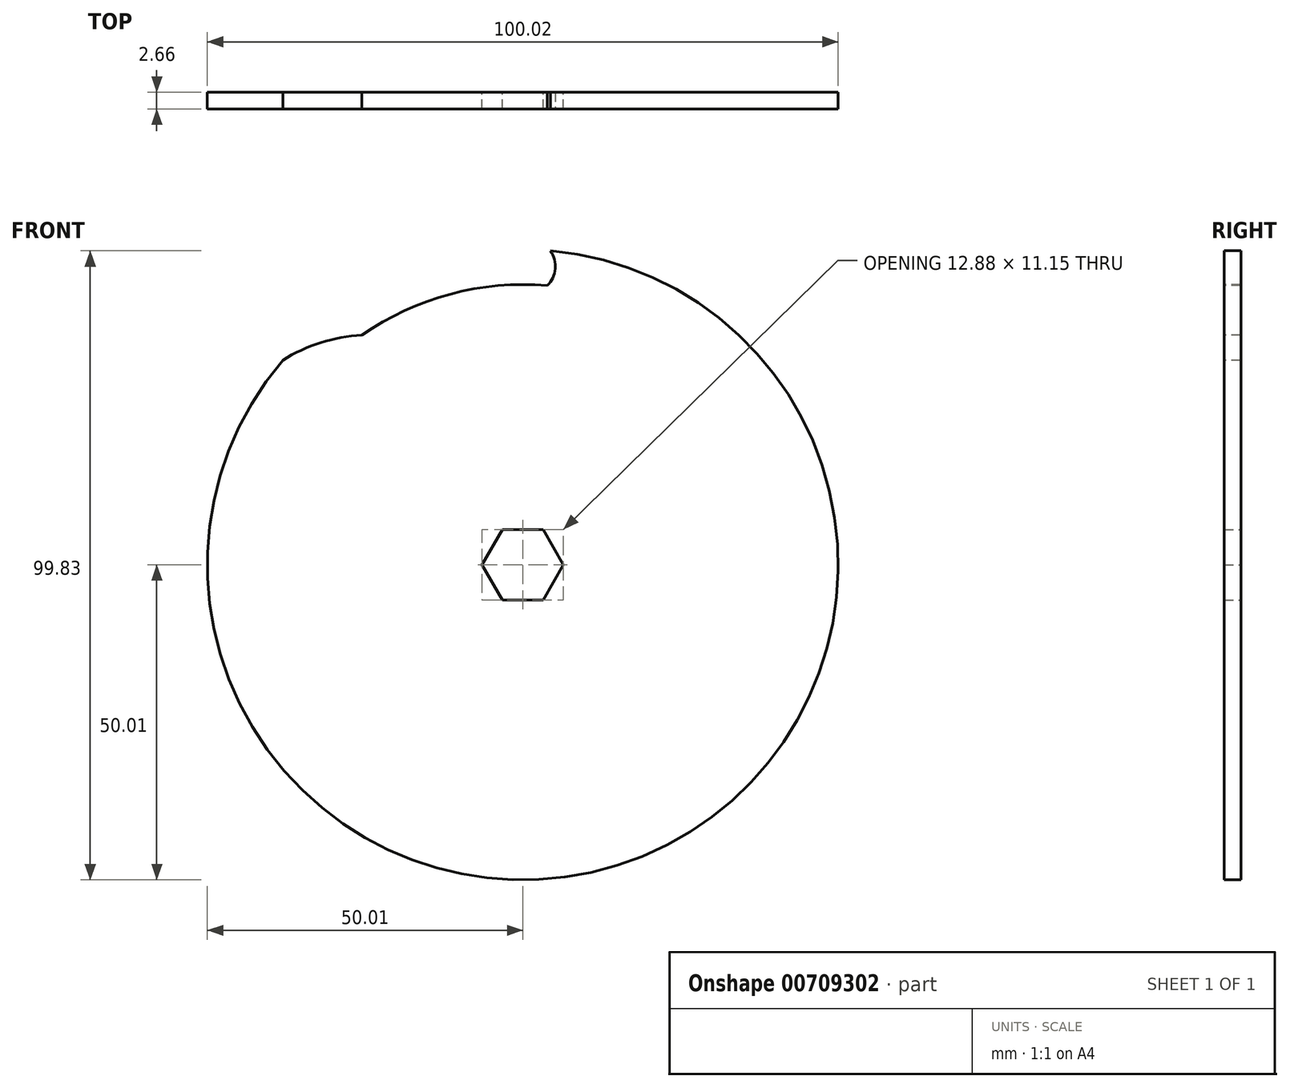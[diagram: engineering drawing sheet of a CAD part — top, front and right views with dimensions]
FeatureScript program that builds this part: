
annotation { "Feature Type Name" : "Feature", "Feature Type Description" : "" }
export const myFeature = defineFeature(function(context is Context, id is Id, definition is map)
    precondition{}
    {
        {
            var Q0;
            Q0=qCreatedBy(makeId("Front.planeOp"),FACE);
            var sketch = newSketch(context, id + "F0", { "sketchPlane" : qUnion([Q0])});
            skCircle(sketch, "E0", {"center": v(0, 0) * mm, "radius": 50 * mm});
            skCircle(sketch, "E1", {"center": v(0, 0) * mm, "radius": 44.45 * mm, "construction": true});
            skCircle(sketch, "E2", {"center": v(0, 0) * mm, "radius": 47.23 * mm, "construction": true});
            skLineSegment(sketch, "E3", {"start": v(0, 0) * mm, "end": v(3.87, 44.28) * mm, "construction": true});
            skLineSegment(sketch, "E4", {"start": v(3.87, 44.28) * mm, "end": v(4.12, 47.05) * mm, "construction": true});
            skLineSegment(sketch, "E5", {"start": v(4.12, 47.05) * mm, "end": v(4.36, 49.82) * mm, "construction": true});
            skArc(sketch, "E6", {"start": v(3.87, 44.28) * mm, "mid": v(5.15, 46.96) * mm, "end": v(4.36, 49.82) * mm, "construction": true});
            skCircle(sketch, "E7", {"center": v(0, 0) * mm, "radius": 6.38 * mm, "construction": true});
            skLineSegment(sketch, "E8", {"start": v(0, 0) * mm, "end": v(-36.41, 25.5) * mm, "construction": true});
            skLineSegment(sketch, "E9", {"start": v(0, 0) * mm, "end": v(-25.5, 36.41) * mm, "construction": true});
            skLineSegment(sketch, "E10", {"start": v(-36.41, 25.5) * mm, "end": v(-40.96, 28.68) * mm, "construction": true});
            skArc(sketch, "E11", {"start": v(-25.5, 36.41) * mm, "mid": v(-32.03, 35.26) * mm, "end": v(-38.05, 32.45) * mm, "construction": true});
            skCircle(sketch, "E12.cCircle", {"center": v(0, 0) * mm, "radius": 5.58 * mm, "construction": true});
            skLineSegment(sketch, "E12.0", {"start": v(-3.22, 5.58) * mm, "end": v(3.22, 5.58) * mm});
            skLineSegment(sketch, "E12.1", {"start": v(3.22, 5.58) * mm, "end": v(6.44, 0) * mm});
            skLineSegment(sketch, "E12.2", {"start": v(6.44, 0) * mm, "end": v(3.22, -5.58) * mm});
            skLineSegment(sketch, "E12.3", {"start": v(3.22, -5.58) * mm, "end": v(-3.22, -5.58) * mm});
            skLineSegment(sketch, "E12.4", {"start": v(-3.22, -5.58) * mm, "end": v(-6.44, 0) * mm});
            skLineSegment(sketch, "E12.5", {"start": v(-6.44, 0) * mm, "end": v(-3.22, 5.58) * mm});
            skPoint(sketch, "E12.0.midPoint", {"position": v(0, 5.58) * mm});
            skLineSegment(sketch, "E13", {"start": v(0, 0) * mm, "end": v(0, 44.45) * mm, "construction": true});
            skSolve(sketch);
        }
        {
            var Q0;
            Q0=qSketchRegion(id+"F0",true);
            extrude(context, id + "F1", {"entities" : qUnion([Q0]), "depth" : 2.67 * mm, "offsetDistance" : 25.4 * mm, "symmetric" : true});
        }
        {
            var Q0;
            Q0=qCreatedBy(makeId("Front.planeOp"),FACE);
            var sketch = newSketch(context, id + "F2", { "sketchPlane" : qUnion([Q0])});
            skArc(sketch, "E14", {"start": v(3.87, 44.28) * mm, "mid": v(-11.5, 42.94) * mm, "end": v(-25.5, 36.41) * mm});
            skArc(sketch, "E15", {"start": v(3.87, 44.28) * mm, "mid": v(5.15, 46.96) * mm, "end": v(4.36, 49.82) * mm});
            skArc(sketch, "E16", {"start": v(-25.5, 36.41) * mm, "mid": v(-32.03, 35.26) * mm, "end": v(-38.05, 32.45) * mm});
            skArc(sketch, "E17", {"start": v(4.36, 49.82) * mm, "mid": v(-18.95, 46.28) * mm, "end": v(-38.05, 32.45) * mm});
            skLineSegment(sketch, "E18", {"start": v(0, 0) * mm, "end": v(-3.87, 44.28) * mm, "construction": true});
            skSolve(sketch);
        }
        {
            var Q0;
            Q0=qSketchRegion(id+"F2",true);
            extrude(context, id + "F3", {"entities" : qUnion([Q0]), "operationType" : NewBodyOperationType.REMOVE, "oppositeDirection" : true, "depth" : 25.4 * mm, "offsetDistance" : 25.4 * mm, "hasSecondDirection" : true, "secondDirectionOppositeDirection" : false, "secondDirectionDepth" : 25.4 * mm});
        }
    });
